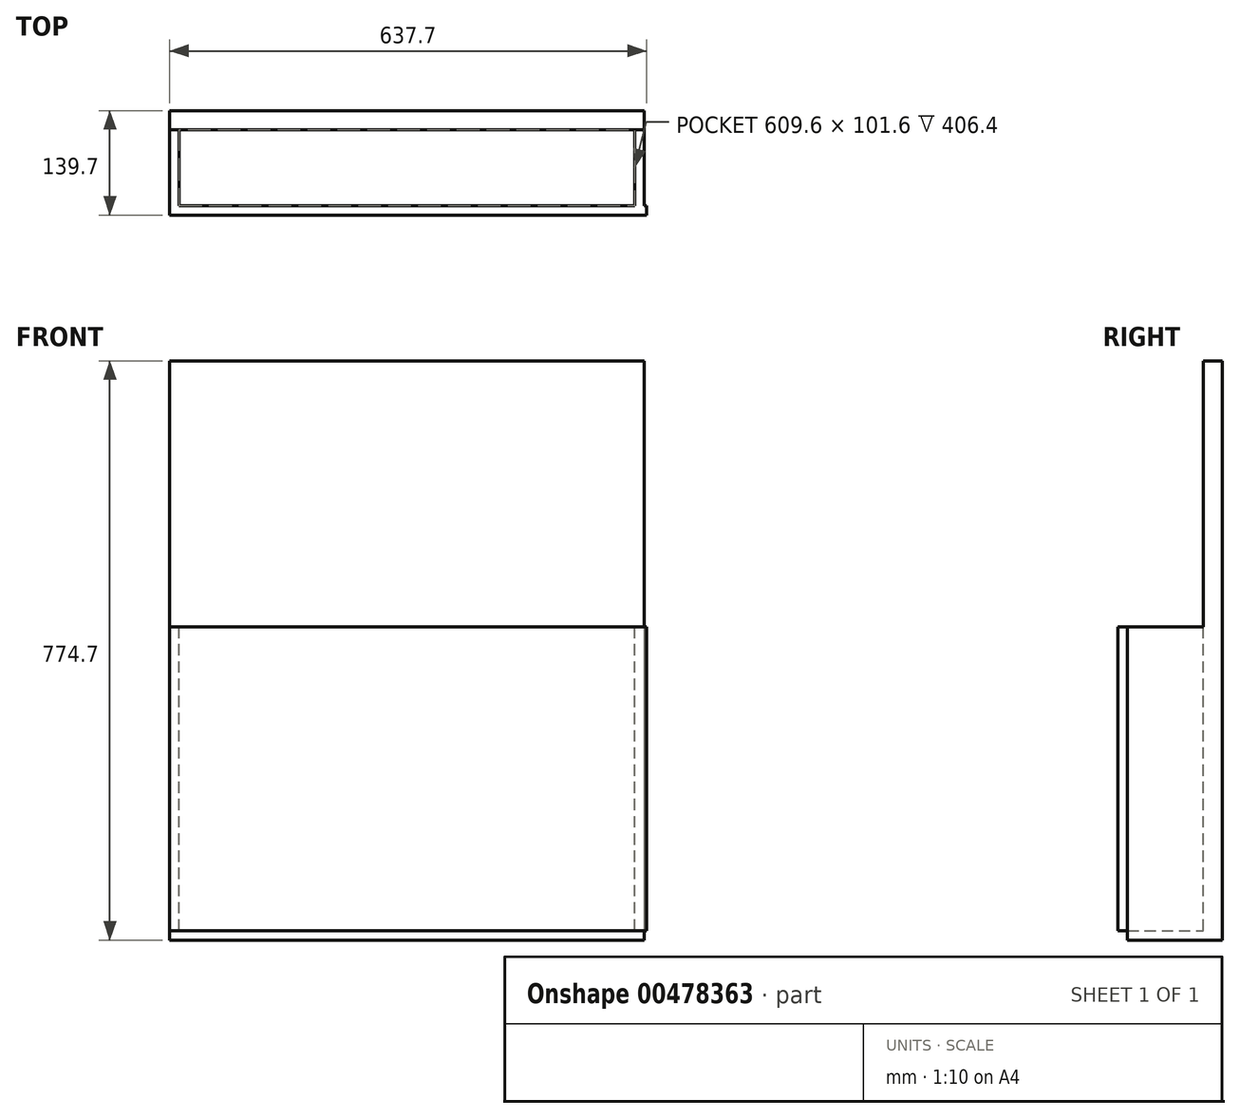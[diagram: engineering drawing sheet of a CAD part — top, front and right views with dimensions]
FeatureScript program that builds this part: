
annotation { "Feature Type Name" : "Feature", "Feature Type Description" : "" }
export const myFeature = defineFeature(function(context is Context, id is Id, definition is map)
    precondition{}
    {
        {
            var Q0;
            Q0=qCreatedBy(makeId("Front.planeOp"),FACE);
            var sketch = newSketch(context, id + "F0", { "sketchPlane" : qUnion([Q0])});
            skLineSegment(sketch, "E0.bottom", {"start": v(-309.5, 176.19) * mm, "end": v(325.5, 176.19) * mm});
            skLineSegment(sketch, "E0.top", {"start": v(-309.5, -585.81) * mm, "end": v(325.5, -585.81) * mm});
            skLineSegment(sketch, "E0.left", {"start": v(-309.5, 176.19) * mm, "end": v(-309.5, -585.81) * mm});
            skLineSegment(sketch, "E0.right", {"start": v(325.5, 176.19) * mm, "end": v(325.5, -585.81) * mm});
            skSolve(sketch);
        }
        {
            var Q0;
            Q0=makeQuery(id+"F0.imprint","IMPRINT",FACE,{"disambiguationData":[TD([[makeQuery(id+"F0.imprint","IMPRINT",EDGE,{"derivedFrom":sQuery(id+"F0.wireOp",EDGE,"E0.bottom")}),-1.0]])]});
            extrude(context, id + "F1", {"entities" : qUnion([Q0]), "depth" : 12.7 * mm});
        }
        {
            var Q0;
            Q0=makeQuery(id+"F1.opExtrude","CAP_FACE",FACE,{"disambiguationData":[OSD([sQuery(id+"F0.wireOp",EDGE,"E0.bottom"),sQuery(id+"F0.wireOp",EDGE,"E0.top"),sQuery(id+"F0.wireOp",EDGE,"E0.left"),sQuery(id+"F0.wireOp",EDGE,"E0.right")])],"isStart":false});
            extrude(context, id + "F2", {"entities" : qUnion([Q0]), "operationType" : NewBodyOperationType.ADD, "depth" : 12.7 * mm, "offsetDistance" : 25.4 * mm});
        }
        {
            var Q0;
            Q0=makeQuery(id+"F2.opExtrude","CAP_FACE",FACE,{"disambiguationData":[OSD([sQuery(id+"F0.wireOp",EDGE,"E0.bottom"),sQuery(id+"F0.wireOp",EDGE,"E0.top"),sQuery(id+"F0.wireOp",EDGE,"E0.left"),sQuery(id+"F0.wireOp",EDGE,"E0.right")])],"isStart":false});
            var sketch = newSketch(context, id + "F3", { "sketchPlane" : qUnion([Q0])});
            skLineSegment(sketch, "E1", {"start": v(-309.5, -585.81) * mm, "end": v(-296.8, -585.81) * mm});
            skLineSegment(sketch, "E2", {"start": v(-296.8, -585.81) * mm, "end": v(-296.8, -179.41) * mm});
            skLineSegment(sketch, "E3", {"start": v(-296.8, -179.41) * mm, "end": v(-309.5, -179.41) * mm});
            skLineSegment(sketch, "E4", {"start": v(-309.5, -179.41) * mm, "end": v(-309.5, -585.81) * mm});
            skSolve(sketch);
        }
        {
            var Q0;
            Q0=makeQuery(id+"F3.imprint","IMPRINT",FACE,{"disambiguationData":[TD([[makeQuery(id+"F3.imprint","IMPRINT",EDGE,{"derivedFrom":sQuery(id+"F3.wireOp",EDGE,"E1")}),1.0]])]});
            extrude(context, id + "F4", {"entities" : qUnion([Q0]), "operationType" : NewBodyOperationType.ADD, "depth" : 101.6 * mm, "offsetDistance" : 25.4 * mm});
        }
        {
            var Q0;
            Q0=makeQuery(id+"F2.opExtrude","CAP_FACE",FACE,{"disambiguationData":[OSD([sQuery(id+"F0.wireOp",EDGE,"E0.bottom"),sQuery(id+"F0.wireOp",EDGE,"E0.top"),sQuery(id+"F0.wireOp",EDGE,"E0.left"),sQuery(id+"F0.wireOp",EDGE,"E0.right")])],"isStart":false});
            var sketch = newSketch(context, id + "F5", { "sketchPlane" : qUnion([Q0])});
            skLineSegment(sketch, "E5", {"start": v(325.5, -585.81) * mm, "end": v(312.8, -585.81) * mm});
            skLineSegment(sketch, "E6", {"start": v(312.8, -585.81) * mm, "end": v(312.8, -179.41) * mm});
            skLineSegment(sketch, "E7", {"start": v(312.8, -179.41) * mm, "end": v(325.5, -179.41) * mm});
            skLineSegment(sketch, "E8", {"start": v(325.5, -179.41) * mm, "end": v(325.5, -585.81) * mm});
            skSolve(sketch);
        }
        {
            var Q0;
            Q0=makeQuery(id+"F5.imprint","IMPRINT",FACE,{"disambiguationData":[TD([[makeQuery(id+"F5.imprint","IMPRINT",EDGE,{"derivedFrom":sQuery(id+"F5.wireOp",EDGE,"E5")}),1.0]])]});
            extrude(context, id + "F6", {"entities" : qUnion([Q0]), "operationType" : NewBodyOperationType.ADD, "depth" : 101.6 * mm, "offsetDistance" : 25.4 * mm});
        }
        {
            var Q0;
            Q0=makeQuery(id+"F4.opExtrude","CAP_FACE",FACE,{"disambiguationData":[OSD([sQuery(id+"F3.wireOp",EDGE,"E1"),sQuery(id+"F3.wireOp",EDGE,"E2"),sQuery(id+"F3.wireOp",EDGE,"E3"),sQuery(id+"F3.wireOp",EDGE,"E4")])],"isStart":false});
            var sketch = newSketch(context, id + "F7", { "sketchPlane" : qUnion([Q0])});
            skLineSegment(sketch, "E9", {"start": v(-309.5, -179.41) * mm, "end": v(328.2, -179.41) * mm});
            skLineSegment(sketch, "E10", {"start": v(328.2, -179.41) * mm, "end": v(328.2, -586.07) * mm});
            skLineSegment(sketch, "E11", {"start": v(328.2, -586.07) * mm, "end": v(-309.5, -585.81) * mm});
            skLineSegment(sketch, "E12", {"start": v(-309.5, -585.81) * mm, "end": v(-309.5, -179.41) * mm});
            skSolve(sketch);
        }
        {
            var Q0;
            Q0 = qSketchRegion(id + "F7", true);
            extrude(context, id + "F8", {"entities" : qUnion([Q0]), "operationType" : NewBodyOperationType.ADD, "depth" : 12.7 * mm, "offsetDistance" : 25.4 * mm});
        }
        {
            var Q0;
            {var subQ0=sQuery(id+"F0.wireOp",EDGE,"E0.top");Q0=makeQuery(id+"F6.boolean.opBoolean","MERGE",FACE,{"derivedFrom":[makeQuery(id+"F4.boolean.opBoolean","MERGE",FACE,{"derivedFrom":[makeQuery(id+"F2.boolean.opBoolean","MERGE",FACE,{"derivedFrom":[makeQuery(id+"F1.opExtrude","SWEPT_FACE",FACE,{"disambiguationData":[OSD([subQ0])]}),makeQuery(id+"F2.opExtrude","SWEPT_FACE",FACE,{"disambiguationData":[OSD([subQ0])]})]}),makeQuery(id+"F4.opExtrude","SWEPT_FACE",FACE,{"disambiguationData":[OSD([sQuery(id+"F3.wireOp",EDGE,"E1")])]})]}),makeQuery(id+"F6.opExtrude","SWEPT_FACE",FACE,{"disambiguationData":[OSD([sQuery(id+"F5.wireOp",EDGE,"E5")])]})]});}
            var sketch = newSketch(context, id + "F9", { "sketchPlane" : qUnion([Q0])});
            skLineSegment(sketch, "E13", {"start": v(325.5, 0) * mm, "end": v(325.5, 127) * mm});
            skLineSegment(sketch, "E14", {"start": v(325.5, 127) * mm, "end": v(-309.5, 127) * mm});
            skLineSegment(sketch, "E15", {"start": v(-309.5, 127) * mm, "end": v(-309.5, 0) * mm});
            skLineSegment(sketch, "E16", {"start": v(-309.5, 0) * mm, "end": v(325.5, 0) * mm});
            skSolve(sketch);
        }
        {
            var Q0;
            Q0 = qSketchRegion(id + "F9", true);
            extrude(context, id + "F10", {"entities" : qUnion([Q0]), "operationType" : NewBodyOperationType.ADD, "depth" : 12.7 * mm, "offsetDistance" : 25.4 * mm});
        }
    });
